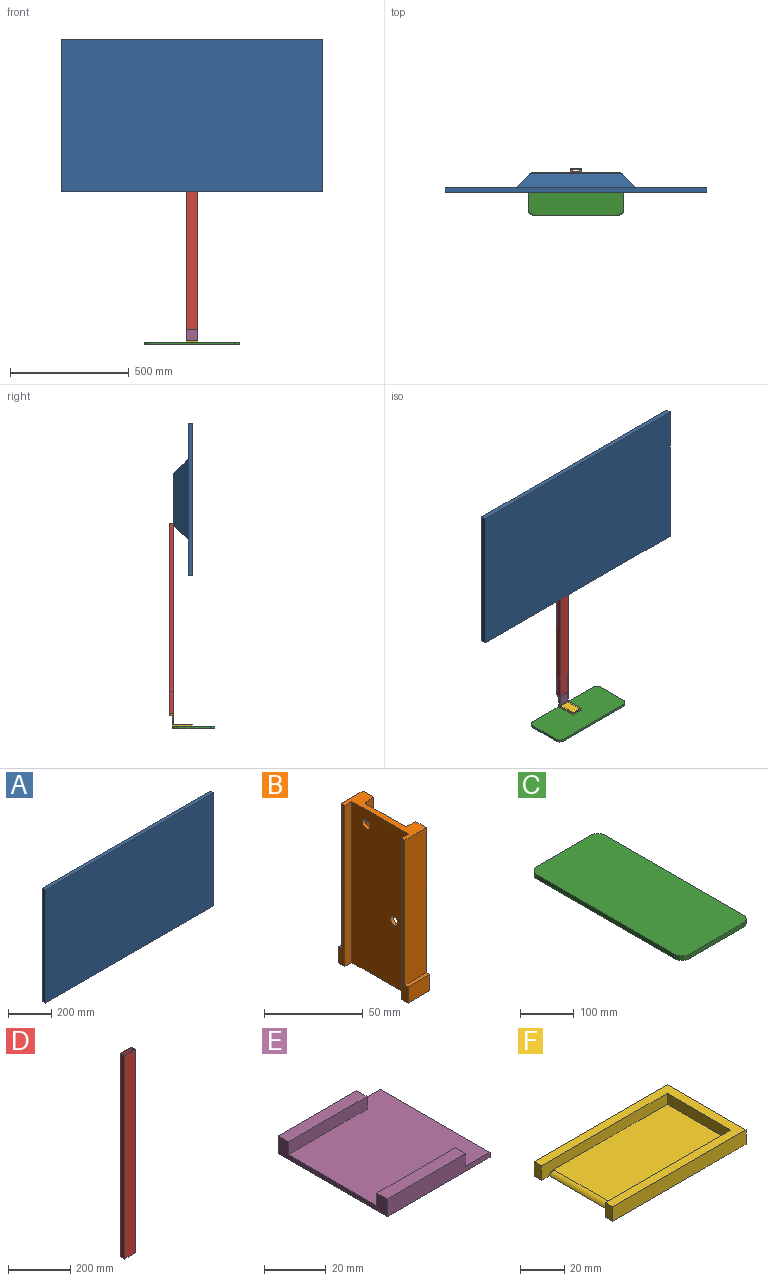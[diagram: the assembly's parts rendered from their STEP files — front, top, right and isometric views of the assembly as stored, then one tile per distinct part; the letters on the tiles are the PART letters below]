
ASSEMBLY  parts=6 mates=5
PART A: 11 faces, bbox 1100x80x640 mm
  f0: plane 380x220mm, normal (0,1,0), area 83600mm2, adj f3,f4,f9,f10
  f1: plane 1100x20mm, normal (0,0,1), area 22000mm2, adj f5,f6,f7,f8
  f2: plane 1100x20mm, normal (0,0,-1), area 22000mm2, adj f5,f6,f7,f8
  f3: plane 340x60mm, normal (0.71,0.71,0), area 23758.8mm2, adj f0,f8,f9,f10
  f4: plane 340x60mm, normal (-0.71,0.71,0), area 23758.8mm2, adj f0,f8,f9,f10
  f5: plane 640x20mm, normal (1,0,0), area 12800mm2, adj f1,f2,f7,f8
  f6: plane 640x20mm, normal (-1,0,0), area 12800mm2, adj f1,f2,f7,f8
  f7: plane 1100x640mm, normal (0,-1,0), area 704000mm2, adj f1,f2,f5,f6
  f8: plane 1100x640mm, normal (0,1,0), area 534000mm2, adj f1,f2,f3,f4,f5,f6,f9,f10
  f9: plane 500x60mm, normal (0,0.71,-0.71), area 37335.2mm2, adj f0,f3,f4,f8
  f10: plane 500x60mm, normal (0,0.71,0.71), area 37335.2mm2, adj f0,f3,f4,f8
PART B: 36 faces, bbox 15.5x50x100 mm
  f0: plane 100x26mm, normal (1,0,0), area 2474mm2, adj f1,f5,f7,f20,f23,f24,f25,f26
  f1: cylinder r=2mm len=100mm, axis (0,0,1), area 305.5mm2, adj f0,f5,f7,f21,f32,f33,f34
  f2: cylinder r=2.75mm len=5.5mm, axis (-1,0,0), area 34.6mm2, adj f17,f35
  f3: cylinder r=2.75mm len=5.5mm, axis (-1,0,0), area 34.6mm2, adj f17,f28
  f4: plane 100x10mm, normal (1,0,0), area 797.5mm2, adj f5,f7,f10,f14,f15,f21
  f5: plane 45.5x15.5mm, normal (0,0,1), area 294.5mm2, adj f0,f1,f4,f6,f8,f9,f12,f14
  f6: plane 100x4.75mm, normal (-1,0,0), area 272.5mm2, adj f5,f7,f10,f14,f15,f16
  f7: plane 50x15.5mm, normal (0,0,-1), area 364.2mm2, adj f0,f1,f4,f6,f8,f9,f10,f11
  f8: plane 100x4.75mm, normal (-1,0,0), area 272.5mm2, adj f5,f7,f11,f12,f13,f18
  f9: plane 100x10mm, normal (1,0,0), area 797.5mm2, adj f5,f7,f11,f12,f13,f19
  f10: plane 15.5x10mm, normal (0,-1,0), area 155mm2, adj f4,f6,f7,f15
  f11: plane 15.5x10mm, normal (0,1,0), area 155mm2, adj f7,f8,f9,f13
  f12: plane 90x15.5mm, normal (0,1,0), area 1395mm2, adj f5,f8,f9,f13
  f13: plane 15.5x2.25mm, normal (0,0,1), area 34.9mm2, adj f8,f9,f11,f12
  f14: plane 90x15.5mm, normal (0,-1,0), area 1395mm2, adj f4,f5,f6,f15
  f15: plane 15.5x2.25mm, normal (0,0,1), area 34.9mm2, adj f4,f6,f10,f14
  f16: plane 100x5mm, normal (0,1,0), area 500mm2, adj f5,f6,f7,f17
  f17: plane 100x40.5mm, normal (-1,0,0), area 4002.5mm2, adj f2,f3,f5,f7,f16,f18
  f18: plane 100x5mm, normal (0,-1,0), area 500mm2, adj f5,f7,f8,f17
  f19: plane 100x5mm, normal (0,-1,0), area 500mm2, adj f5,f7,f9,f20
  f20: cylinder r=2mm len=100mm, axis (0,0,1), area 305.5mm2, adj f0,f5,f7,f19,f22,f23,f24
  f21: plane 100x5mm, normal (0,1,0), area 500mm2, adj f1,f4,f5,f7
  f22: plane 8x1.77mm, normal (0,-1,0), area 14.1mm2, adj f20,f23,f24,f28
  f23: plane 4.01x1.78mm, normal (0,-0.22,0.98), area 6.2mm2, adj f0,f20,f22,f27,f28
  f24: plane 4.01x1.78mm, normal (0,-0.22,-0.98), area 6.2mm2, adj f0,f20,f22,f25,f28
  f25: plane 4x1.5mm, normal (0,0.22,-0.98), area 6.1mm2, adj f0,f24,f26,f28
  f26: plane 8x1.5mm, normal (0,1,0), area 12mm2, adj f0,f25,f27,f28
  f27: plane 4x1.5mm, normal (0,0.22,0.98), area 6.1mm2, adj f0,f23,f26,f28
  f28: plane 9.8x8mm, normal (1,0,0), area 47.4mm2, adj f3,f22,f23,f24,f25,f26,f27
  f29: plane 4x1.5mm, normal (0,-0.22,0.98), area 6.1mm2, adj f0,f30,f34,f35
  f30: plane 8x1.5mm, normal (0,-1,0), area 12mm2, adj f0,f29,f31,f35
  f31: plane 4x1.5mm, normal (0,-0.22,-0.98), area 6.1mm2, adj f0,f30,f32,f35
  f32: plane 4.01x1.78mm, normal (0,0.22,-0.98), area 6.2mm2, adj f0,f1,f31,f33,f35
  f33: plane 8x1.77mm, normal (0,1,0), area 14.1mm2, adj f1,f32,f34,f35
  f34: plane 4.01x1.78mm, normal (0,0.22,0.98), area 6.2mm2, adj f0,f1,f29,f33,f35
  f35: plane 9.8x8mm, normal (1,0,0), area 47.4mm2, adj f2,f29,f30,f31,f32,f33,f34
PART C: 10 faces, bbox 180x400x10 mm
  f0: cylinder r=20mm len=20mm, axis (0,0,-1), area 314.2mm2, adj f1,f7,f8,f9
  f1: plane 140x10mm, normal (0,-1,0), area 1400mm2, adj f0,f2,f8,f9
  f2: cylinder r=20mm len=20mm, axis (0,0,-1), area 314.2mm2, adj f1,f3,f8,f9
  f3: plane 360x10mm, normal (1,0,0), area 3600mm2, adj f2,f4,f8,f9
  f4: cylinder r=20mm len=20mm, axis (0,0,-1), area 314.2mm2, adj f3,f5,f8,f9
  f5: plane 140x10mm, normal (0,1,0), area 1400mm2, adj f4,f6,f8,f9
  f6: cylinder r=20mm len=20mm, axis (0,0,-1), area 314.2mm2, adj f5,f7,f8,f9
  f7: plane 360x10mm, normal (-1,0,0), area 3600mm2, adj f0,f6,f8,f9
  f8: plane 400x180mm, normal (0,0,1), area 71656.6mm2, adj f0,f1,f2,f3,f4,f5,f6,f7
  f9: plane 400x180mm, normal (0,0,-1), area 71656.6mm2, adj f0,f1,f2,f3,f4,f5,f6,f7
PART D: 10 faces, bbox 50x20x800 mm
  f0: plane 800x16mm, normal (1,0,0), area 12800mm2, adj f1,f7,f8,f9
  f1: plane 800x46mm, normal (0,-1,0), area 36800mm2, adj f0,f2,f8,f9
  f2: plane 800x16mm, normal (-1,0,0), area 12800mm2, adj f1,f7,f8,f9
  f3: plane 800x50mm, normal (0,1,0), area 40000mm2, adj f4,f6,f8,f9
  f4: plane 800x20mm, normal (-1,0,0), area 16000mm2, adj f3,f5,f8,f9
  f5: plane 800x50mm, normal (0,-1,0), area 40000mm2, adj f4,f6,f8,f9
  f6: plane 800x20mm, normal (1,0,0), area 16000mm2, adj f3,f5,f8,f9
  f7: plane 800x46mm, normal (0,1,0), area 36800mm2, adj f0,f2,f8,f9
  f8: plane 50x20mm, normal (0,0,1), area 264mm2, adj f0,f1,f2,f3,f4,f5,f6,f7
  f9: plane 50x20mm, normal (0,0,-1), area 264mm2, adj f0,f1,f2,f3,f4,f5,f6,f7
PART E: 12 faces, bbox 47x50x7 mm
  f0: plane 50x2mm, normal (1,0,0), area 100mm2, adj f1,f4,f6,f9
  f1: plane 47x7mm, normal (0,1,0), area 274mm2, adj f0,f2,f3,f6,f9,f10
  f2: plane 36x4.75mm, normal (0,0,1), area 171mm2, adj f1,f3,f8,f10
  f3: plane 50x7mm, normal (-1,0,0), area 147.5mm2, adj f1,f2,f4,f5,f6,f7,f8,f9
  f4: plane 47x7mm, normal (0,-1,0), area 274mm2, adj f0,f3,f5,f6,f9,f11
  f5: plane 36x4.75mm, normal (0,0,1), area 171mm2, adj f3,f4,f7,f11
  f6: plane 50x47mm, normal (0,0,-1), area 2350mm2, adj f0,f1,f3,f4
  f7: plane 36x5mm, normal (0,1,0), area 180mm2, adj f3,f5,f9,f11
  f8: plane 36x5mm, normal (0,-1,0), area 180mm2, adj f2,f3,f9,f10
  f9: plane 50x47mm, normal (0,0,1), area 2008mm2, adj f0,f1,f3,f4,f7,f8,f10,f11
  f10: plane 5x4.75mm, normal (1,0,0), area 23.8mm2, adj f1,f2,f8,f9
  f11: plane 5x4.75mm, normal (1,0,0), area 23.8mm2, adj f4,f5,f7,f9
PART F: 12 faces, bbox 85x50x8 mm
  f0: plane 8x4.75mm, normal (-1,0,0), area 38mm2, adj f1,f4,f6,f8
  f1: plane 85x50mm, normal (0,0,-1), area 4047.5mm2, adj f0,f3,f5,f6,f7,f8,f9,f11
  f2: plane 72.17x40.5mm, normal (0,0,1), area 2922.9mm2, adj f8,f9,f10,f11
  f3: plane 8x4.75mm, normal (-1,0,0), area 38mm2, adj f1,f4,f5,f9
  f4: plane 85x50mm, normal (0,0,1), area 1010mm2, adj f0,f3,f5,f6,f7,f8,f9,f10
  f5: plane 85x8mm, normal (0,1,0), area 680mm2, adj f1,f3,f4,f7
  f6: plane 85x8mm, normal (0,-1,0), area 680mm2, adj f0,f1,f4,f7
  f7: plane 50x8mm, normal (1,0,0), area 400mm2, adj f1,f4,f5,f6
  f8: plane 80x8mm, normal (0,1,0), area 491.5mm2, adj f0,f1,f2,f4,f10,f11
  f9: plane 80x8mm, normal (0,-1,0), area 491.5mm2, adj f1,f2,f3,f4,f10,f11
  f10: plane 40.5x6mm, normal (-1,0,0), area 243mm2, adj f2,f4,f8,f9
  f11: cylinder r=3mm len=40.5mm, axis (0,1,0), area 149.6mm2, adj f1,f2,f8,f9
PLACE A rot(axis=(-0.26,-0.33,-0.91),0deg) t=(2033.46,-47,645)mm
PLACE B rot(axis=(0,0,1),90deg) t=(0,649.69,55)mm
PLACE C rot(axis=(0,0,1),90deg) t=(0,363.6,0)mm
PLACE D rot(axis=(0,-1,0),180deg) t=(-975.54,3,865)mm
PLACE E rot(axis=(-0.58,-0.58,-0.58),120deg) t=(0,-7,770.17)mm
PLACE F rot(axis=(0.71,-0.71,0),180deg) t=(0,-859.9,18)mm
MATE fastened F.f1 <-> E.f3  axis (0,0,1) through (-25,0,18)mm
MATE slider D.f8 <-> E.f0  axis (0,0,-1) through (-25,-7,65)mm
MATE fastened E.f9 <-> B.f6  axis (0,1,0) through (25,-5,65)mm
MATE fastened C.f8 <-> F.f4  axis (0,0,1) through (0,0,10)mm
MATE fastened A.f0 <-> D.f5  axis (0,1,0) through (0,-7,965)mm
